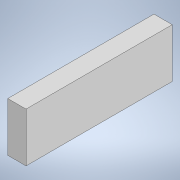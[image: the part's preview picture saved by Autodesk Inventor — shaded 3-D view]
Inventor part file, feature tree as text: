
AUTODESK INVENTOR PART (.ipt)
format: ipt  version: 2021 (Build 250183000, 183)  size: 87,040 bytes
history: native  units: mm
features: other x1, extrude x1, sketch x1
ambient origin geometry x8: Origin, YZ Plane, XZ Plane, XY Plane, X Axis, Y Axis, Z Axis, Center Point
bodies: Body1 (feature_tree)
feature tree (3):
  other  "Твердое тело1"
  extrude  "Выдавливание1"  Depth=160.0mm
  sketch  "Эскиз1"
